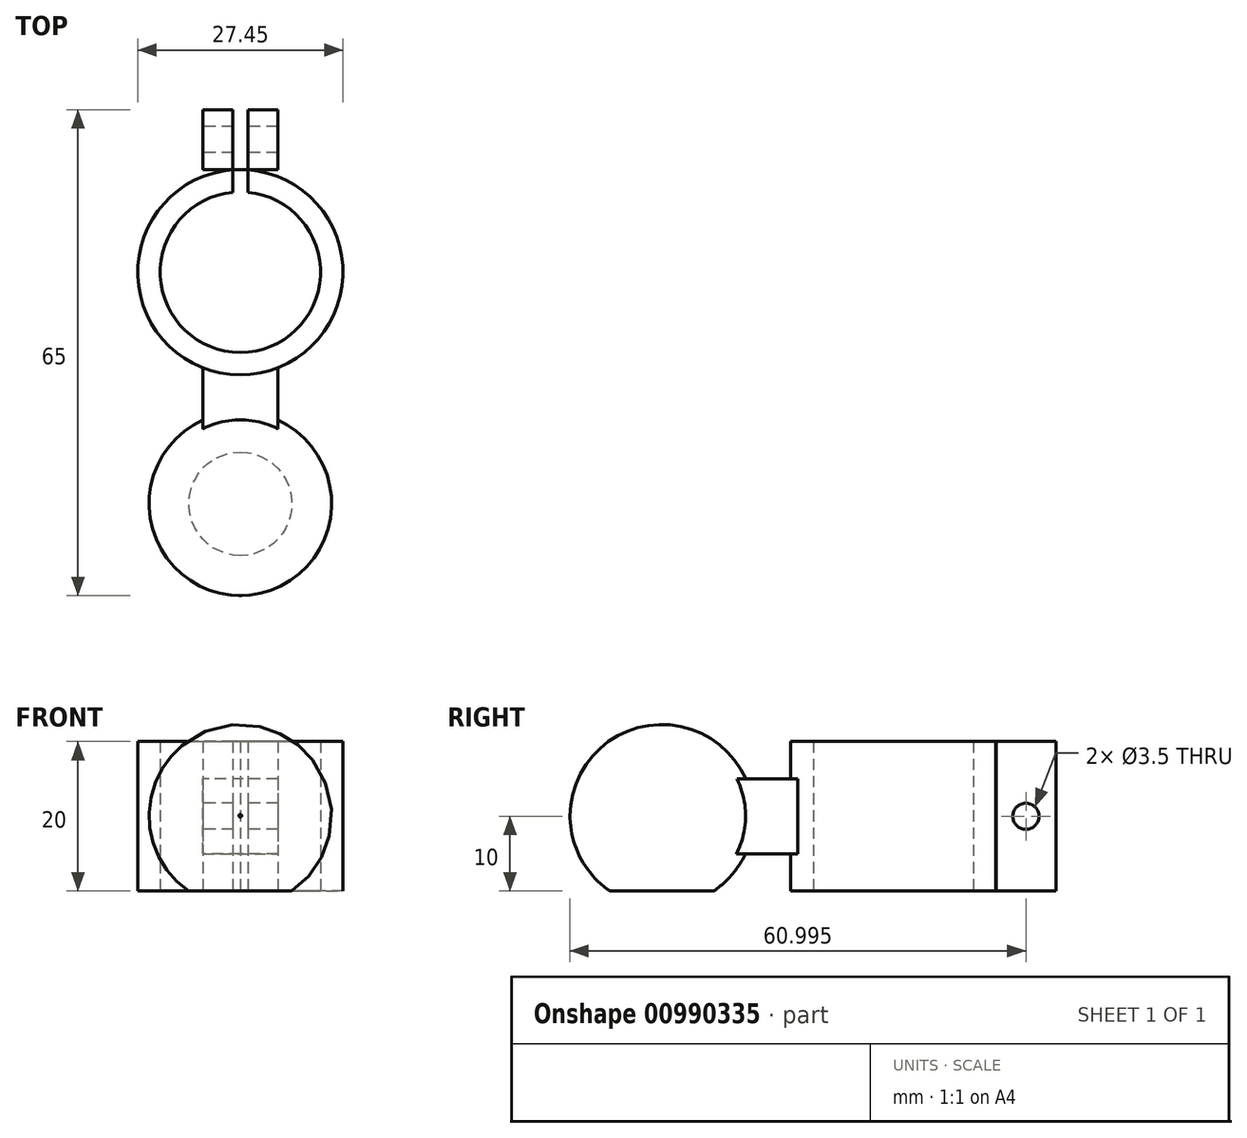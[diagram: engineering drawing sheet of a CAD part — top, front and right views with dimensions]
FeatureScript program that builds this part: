
annotation { "Feature Type Name" : "Feature", "Feature Type Description" : "" }
export const myFeature = defineFeature(function(context is Context, id is Id, definition is map)
    precondition{}
    {
        {
            var Q0;
            Q0=qCreatedBy(makeId("Top.planeOp"),FACE);
            var sketch = newSketch(context, id + "F0", { "sketchPlane" : qUnion([Q0])});
            skCircle(sketch, "E0", {"center": v(0, 0) * mm, "radius": 10.72 * mm});
            skCircle(sketch, "E1", {"center": v(0, 0) * mm, "radius": 13.72 * mm});
            skLineSegment(sketch, "E2", {"start": v(0, 13.72) * mm, "end": v(-5, 13.72) * mm});
            skLineSegment(sketch, "E3", {"start": v(0, 13.72) * mm, "end": v(5, 13.72) * mm});
            skLineSegment(sketch, "E4", {"start": v(-5, 13.72) * mm, "end": v(-5, 12.78) * mm});
            skLineSegment(sketch, "E5", {"start": v(5, 13.72) * mm, "end": v(5, 12.78) * mm});
            skLineSegment(sketch, "E6", {"start": v(0, 13.72) * mm, "end": v(-1, 13.72) * mm});
            skLineSegment(sketch, "E7", {"start": v(-1, 13.72) * mm, "end": v(-1, 10.68) * mm});
            skLineSegment(sketch, "E8", {"start": v(-1, 10.68) * mm, "end": v(0, 10.68) * mm});
            skLineSegment(sketch, "E9", {"start": v(0, 10.68) * mm, "end": v(1, 10.68) * mm});
            skLineSegment(sketch, "E10", {"start": v(1, 10.68) * mm, "end": v(1, 13.72) * mm});
            skLineSegment(sketch, "E11", {"start": v(1, 13.72) * mm, "end": v(0, 13.72) * mm});
            skLineSegment(sketch, "E12", {"start": v(-5, 13.72) * mm, "end": v(-5, 21.73) * mm});
            skLineSegment(sketch, "E13", {"start": v(5, 13.72) * mm, "end": v(5, 21.73) * mm});
            skLineSegment(sketch, "E14", {"start": v(5, 21.73) * mm, "end": v(-5, 21.73) * mm});
            skLineSegment(sketch, "E15", {"start": v(-1, 13.72) * mm, "end": v(-1, 21.73) * mm});
            skLineSegment(sketch, "E16", {"start": v(1, 13.72) * mm, "end": v(1, 21.73) * mm});
            skSolve(sketch);
        }
        {
            var Q0;
            {var subQ0=sQuery(id+"F0.wireOp",EDGE,"E1");var subQ8=makeQuery(id+"F0.imprint","INTERSECT",VERTEX,{"derivedFrom":[subQ0,sQuery(id+"F0.wireOp",EDGE,"E5")]});Q0=makeQuery(id+"F0.imprint","IMPRINT",FACE,{"disambiguationData":[TD([[makeQuery(id+"F0.imprint","IMPRINT",EDGE,{"disambiguationData":[TD([[subQ8,-1.0]])],"derivedFrom":subQ0}),1.0]])]});}
            var Q1;
            Q1=makeQuery(id+"F0.imprint","IMPRINT",FACE,{"disambiguationData":[TD([[makeQuery(id+"F0.imprint","IMPRINT",EDGE,{"derivedFrom":sQuery(id+"F0.wireOp",EDGE,"E2")}),-1.0]])]});
            var Q2;
            {var subQ4=sQuery(id+"F0.wireOp",EDGE,"E2");Q2=makeQuery(id+"F0.imprint","IMPRINT",FACE,{"disambiguationData":[TD([[makeQuery(id+"F0.imprint","IMPRINT",EDGE,{"derivedFrom":subQ4}),1.0]])]});}
            var Q3;
            {var subQ4=sQuery(id+"F0.wireOp",EDGE,"E3");Q3=makeQuery(id+"F0.imprint","IMPRINT",FACE,{"disambiguationData":[TD([[makeQuery(id+"F0.imprint","IMPRINT",EDGE,{"derivedFrom":subQ4}),-1.0]])]});}
            var Q4;
            Q4=makeQuery(id+"F0.imprint","IMPRINT",FACE,{"disambiguationData":[TD([[makeQuery(id+"F0.imprint","IMPRINT",EDGE,{"derivedFrom":sQuery(id+"F0.wireOp",EDGE,"E3")}),1.0]])]});
            extrude(context, id + "F1", {"entities" : qUnion([Q0, Q1, Q2, Q3, Q4]), "depth" : 20 * mm, "offsetDistance" : 25 * mm});
        }
        {
            var Q0;
            Q0=makeQuery(id+"F1.opExtrude","SWEPT_FACE",FACE,{"disambiguationData":[OSD([sQuery(id+"F0.wireOp",EDGE,"E4"),sQuery(id+"F0.wireOp",EDGE,"E12")])]});
            var sketch = newSketch(context, id + "F2", { "sketchPlane" : qUnion([Q0])});
            skLineSegment(sketch, "E17", {"start": v(-21.73, 20) * mm, "end": v(-21.73, 10) * mm});
            skLineSegment(sketch, "E18", {"start": v(-21.73, 10) * mm, "end": v(-17.73, 10) * mm});
            skCircle(sketch, "E19", {"center": v(-17.73, 10) * mm, "radius": 1.75 * mm});
            skSolve(sketch);
        }
        {
            var Q0;
            Q0=makeQuery(id+"F2.imprint","IMPRINT",FACE,{"disambiguationData":[TD([[makeQuery(id+"F2.imprint","IMPRINT",EDGE,{"derivedFrom":sQuery(id+"F2.wireOp",EDGE,"E19")}),1.0]])]});
            extrude(context, id + "F3", {"entities" : qUnion([Q0]), "operationType" : NewBodyOperationType.REMOVE, "oppositeDirection" : true, "depth" : 25 * mm, "offsetDistance" : 25 * mm});
        }
        {
            var Q0;
            Q0=qCreatedBy(makeId("Front.planeOp"),FACE);
            cPlane(context, id + "F4", {"entities" : qUnion([Q0]), "cplaneType" : CPlaneType.OFFSET, "offset" : 13 * mm, "width" : 150 * mm, "height" : 150 * mm});
        }
        {
            var Q0;
            Q0=qCreatedBy(id+"F4.planeOp",FACE);
            var sketch = newSketch(context, id + "F5", { "sketchPlane" : qUnion([Q0])});
            skLineSegment(sketch, "E20", {"start": v(0, 0) * mm, "end": v(0, 5) * mm});
            skLineSegment(sketch, "E21", {"start": v(0, 5) * mm, "end": v(5, 5) * mm});
            skLineSegment(sketch, "E22", {"start": v(5, 5) * mm, "end": v(5, 15) * mm});
            skLineSegment(sketch, "E23", {"start": v(5, 15) * mm, "end": v(-5, 15) * mm});
            skLineSegment(sketch, "E24", {"start": v(-5, 15) * mm, "end": v(-5, 5) * mm});
            skLineSegment(sketch, "E25", {"start": v(-5, 5) * mm, "end": v(0, 5) * mm});
            skSolve(sketch);
        }
        {
            var Q0;
            Q0 = qSketchRegion(id + "F5", true);
            extrude(context, id + "F6", {"entities" : qUnion([Q0]), "operationType" : NewBodyOperationType.ADD, "depth" : 18 * mm, "offsetDistance" : 25 * mm});
        }
        {
            var Q0;
            Q0 = qSketchRegion(id + "F5", true);
            extrude(context, id + "F7", {"entities" : qUnion([Q0]), "operationType" : NewBodyOperationType.ADD, "endBound" : BoundingType.UP_TO_NEXT, "oppositeDirection" : true, "depth" : 25 * mm, "offsetDistance" : 25 * mm});
        }
        {
            var Q0;
            {var subQ0=sQuery(id+"F5.wireOp",EDGE,"E22");Q0=makeQuery(id+"F7.boolean.opBoolean","MERGE",FACE,{"derivedFrom":[makeQuery(id+"F6.opExtrude","SWEPT_FACE",FACE,{"disambiguationData":[OSD([subQ0])]}),makeQuery(id+"F7.opExtrude","SWEPT_FACE",FACE,{"disambiguationData":[OSD([subQ0])]})]});}
            var sketch = newSketch(context, id + "F8", { "sketchPlane" : qUnion([Q0])});
            skSolve(sketch);
        }
        {
            var Q0;
            {var subQ0=sQuery(id+"F5.wireOp",EDGE,"E22");Q0=makeQuery(id+"F8.imprint","IMPRINT",FACE,{"disambiguationData":[TD([[makeQuery(id+"F8.imprint","IMPRINT",EDGE,{"derivedFrom":makeQuery(id+"F6.opExtrude","CAP_EDGE",EDGE,{"disambiguationData":[OSD([subQ0])],"isStart":false})}),-1.0]])]});}
            cPlane(context, id + "F9", {"entities" : qUnion([Q0]), "cplaneType" : CPlaneType.OFFSET, "offset" : 5 * mm, "oppositeDirection" : true, "width" : 150 * mm, "height" : 150 * mm});
        }
        {
            var Q0;
            Q0=qCreatedBy(id+"F9.planeOp",FACE);
            var sketch = newSketch(context, id + "F10", { "sketchPlane" : qUnion([Q0])});
            skPoint(sketch, "E26", {"position": v(-30.97, 10.07) * mm});
            skLineSegment(sketch, "E27", {"start": v(-30.97, 10.07) * mm, "end": v(-43.27, 10.07) * mm});
            skArc(sketch, "E28", {"start": v(-18.67, 10.07) * mm, "mid": v(-30.97, 22.28) * mm, "end": v(-43.27, 10.07) * mm});
            skLineSegment(sketch, "E29", {"start": v(-30.97, 10.07) * mm, "end": v(-18.67, 10.07) * mm});
            skSolve(sketch);
        }
        {
            var Q0;
            Q0=makeQuery(id+"F10.imprint","IMPRINT",FACE,{"disambiguationData":[TD([[makeQuery(id+"F10.imprint","IMPRINT",EDGE,{"derivedFrom":sQuery(id+"F10.wireOp",EDGE,"E27")}),-1.0]])]});
            var Q1;
            Q1=sQuery(id+"F10.wireOp",EDGE,"E27");
            revolve(context, id + "F11", {"operationType" : NewBodyOperationType.ADD, "surfaceOperationType" : NewSurfaceOperationType.NEW, "entities" : qUnion([Q0]), "axis" : qUnion([Q1]), "revolveType" : RevolveType.FULL});
        }
        {
            var Q0;
            Q0=qCreatedBy(makeId("Top.planeOp"),FACE);
            var sketch = newSketch(context, id + "F12", { "sketchPlane" : qUnion([Q0])});
            skLineSegment(sketch, "E30.bottom", {"start": v(-16.7, -52.47) * mm, "end": v(19.27, -52.47) * mm});
            skLineSegment(sketch, "E30.top", {"start": v(-16.7, -15.77) * mm, "end": v(19.27, -15.77) * mm});
            skLineSegment(sketch, "E30.left", {"start": v(-16.7, -52.47) * mm, "end": v(-16.7, -15.77) * mm});
            skLineSegment(sketch, "E30.right", {"start": v(19.27, -52.47) * mm, "end": v(19.27, -15.77) * mm});
            skSolve(sketch);
        }
        {
            var Q0;
            Q0 = qSketchRegion(id + "F12", true);
            extrude(context, id + "F13", {"entities" : qUnion([Q0]), "operationType" : NewBodyOperationType.REMOVE, "oppositeDirection" : true, "depth" : 25 * mm, "offsetDistance" : 25 * mm});
        }
    });
